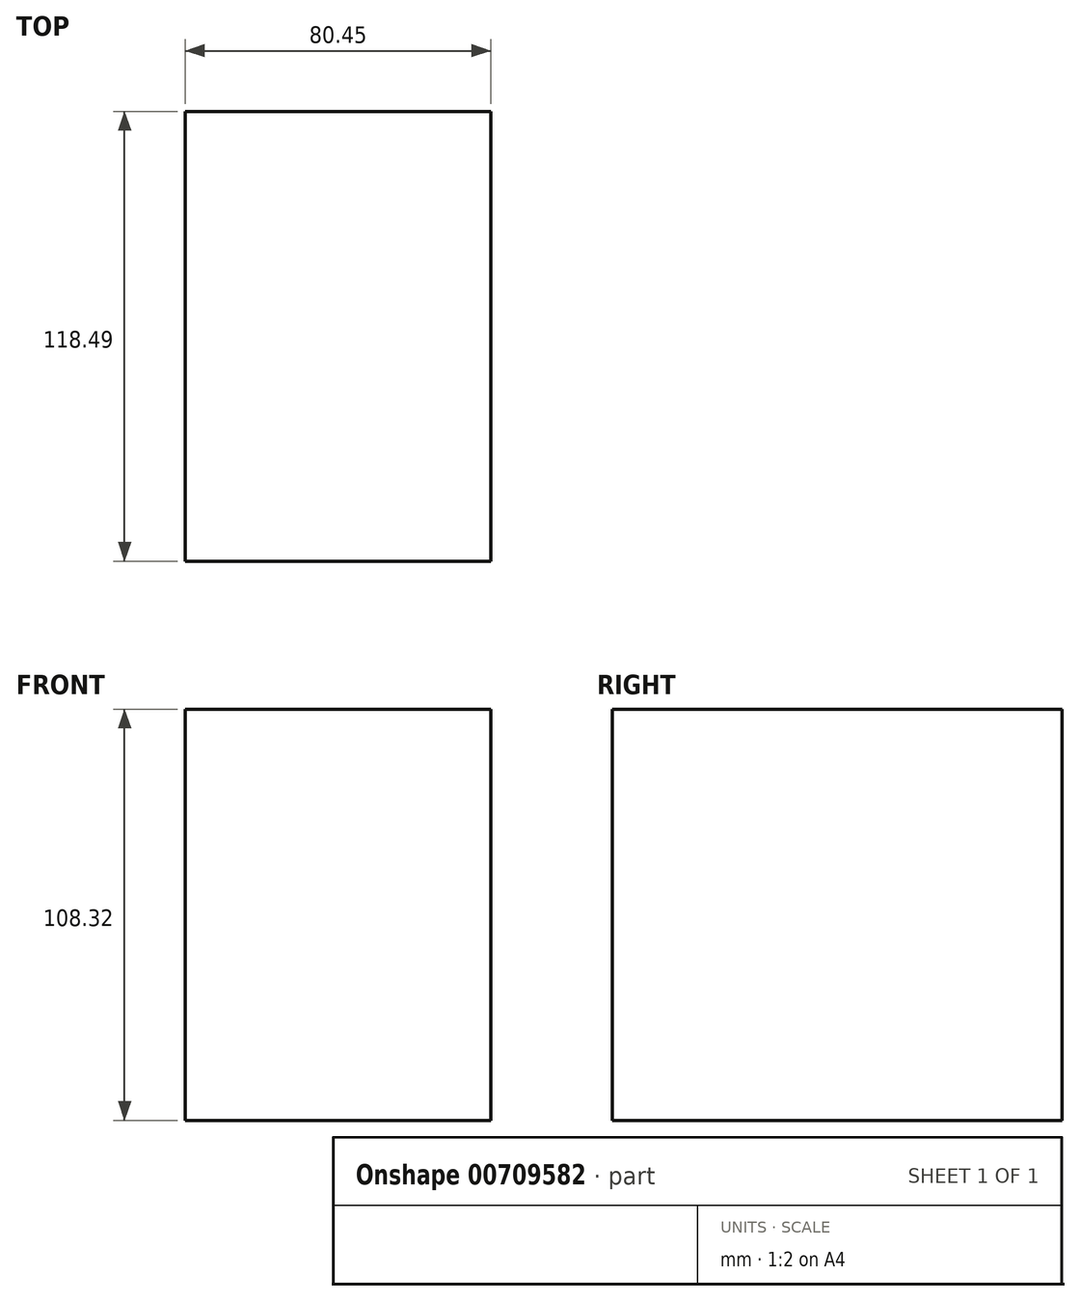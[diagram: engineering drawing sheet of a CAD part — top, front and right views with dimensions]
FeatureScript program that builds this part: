
annotation { "Feature Type Name" : "Feature", "Feature Type Description" : "" }
export const myFeature = defineFeature(function(context is Context, id is Id, definition is map)
    precondition{}
    {
        {
            var Q0;
            Q0=qCreatedBy(makeId("Front.planeOp"),FACE);
            var sketch = newSketch(context, id + "F0", { "sketchPlane" : qUnion([Q0])});
            skLineSegment(sketch, "E0.bottom", {"start": v(22.83, 54.16) * mm, "end": v(-57.62, 54.16) * mm});
            skLineSegment(sketch, "E0.top", {"start": v(22.83, -54.16) * mm, "end": v(-57.62, -54.16) * mm});
            skLineSegment(sketch, "E0.left", {"start": v(22.83, 54.16) * mm, "end": v(22.83, -54.16) * mm});
            skLineSegment(sketch, "E0.right", {"start": v(-57.62, 54.16) * mm, "end": v(-57.62, -54.16) * mm});
            skPoint(sketch, "E0.middle", {"position": v(-17.4, 0) * mm});
            skSolve(sketch);
        }
        {
            var Q0;
            Q0=makeQuery(id+"F0.imprint","IMPRINT",FACE,{"disambiguationData":[TD([[makeQuery(id+"F0.imprint","IMPRINT",EDGE,{"derivedFrom":sQuery(id+"F0.wireOp",EDGE,"E0.bottom")}),1.0]])]});
            var Q1;
            Q1=sQuery(id+"F0.wireOp",EDGE,"E0.top");
            var Q2;
            Q2=sQuery(id+"F0.wireOp",EDGE,"E0.bottom");
            var Q3;
            Q3=sQuery(id+"F0.wireOp",EDGE,"E0.left");
            var Q4;
            Q4=sQuery(id+"F0.wireOp",EDGE,"E0.right");
            extrude(context, id + "F1", {"entities" : qUnion([Q0]), "surfaceEntities" : qUnion([Q1, Q2, Q3, Q4]), "depth" : 118.5 * mm, "offsetDistance" : 25 * mm});
        }
    });
